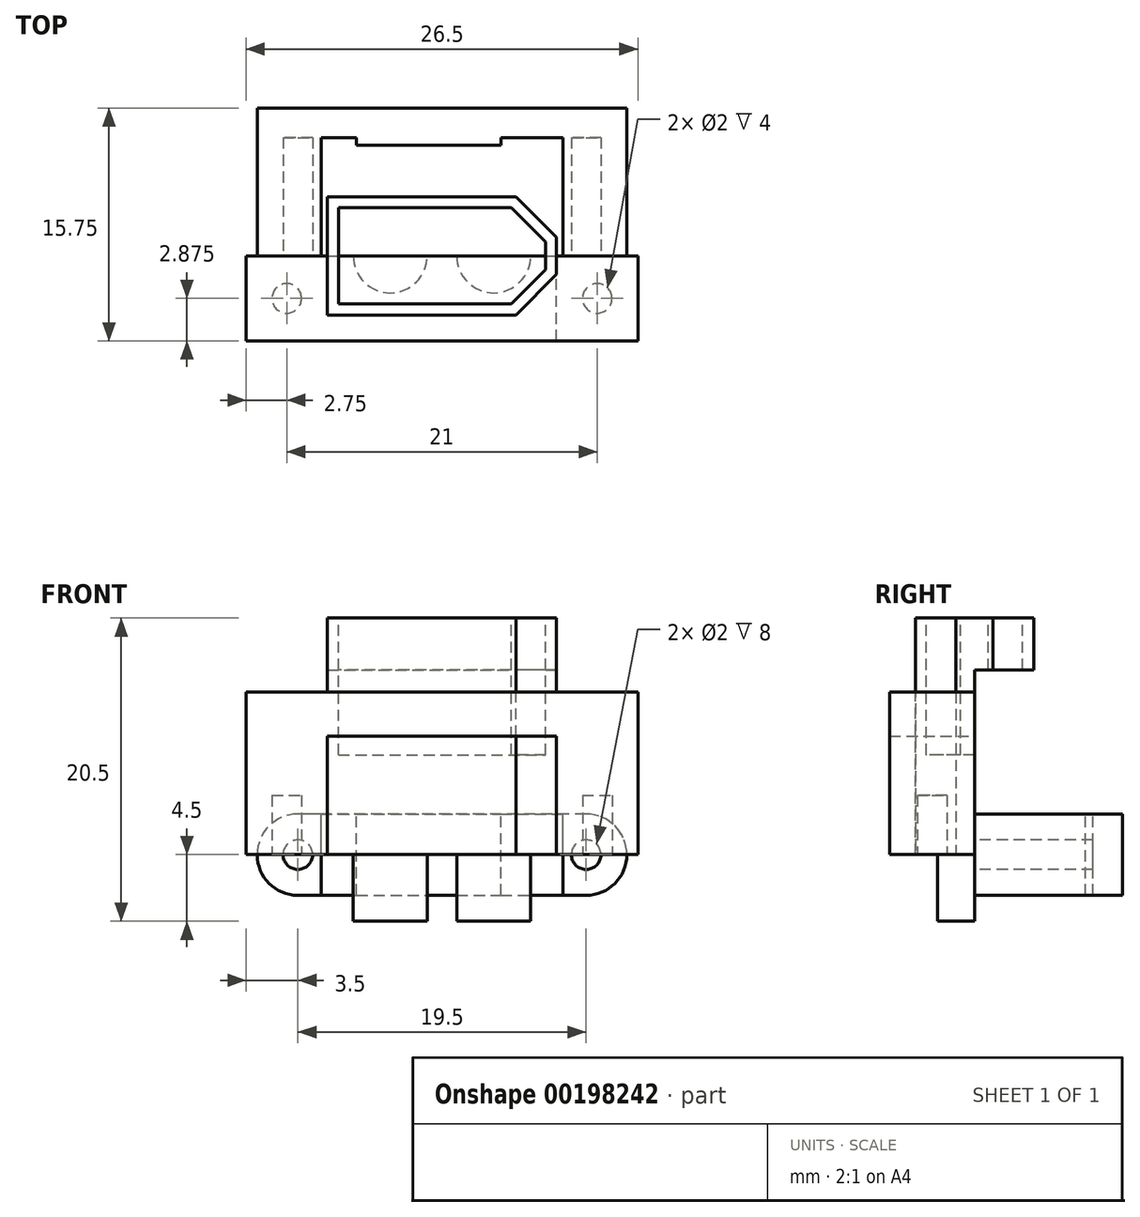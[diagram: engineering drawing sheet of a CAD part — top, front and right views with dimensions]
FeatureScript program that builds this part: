
annotation { "Feature Type Name" : "Feature", "Feature Type Description" : "" }
export const myFeature = defineFeature(function(context is Context, id is Id, definition is map)
    precondition{}
    {
        {
            var Q0;
            Q0=qCreatedBy(makeId("Top.planeOp"),FACE);
            var sketch = newSketch(context, id + "F0", { "sketchPlane" : qUnion([Q0])});
            skLineSegment(sketch, "E0.bottom", {"start": v(-7.75, 4) * mm, "end": v(7.75, 4) * mm});
            skLineSegment(sketch, "E0.top", {"start": v(-7.75, -4) * mm, "end": v(7.75, -4) * mm});
            skLineSegment(sketch, "E0.left", {"start": v(-7.75, 4) * mm, "end": v(-7.75, -4) * mm});
            skLineSegment(sketch, "E0.right", {"start": v(7.75, 4) * mm, "end": v(7.75, -4) * mm});
            skSolve(sketch);
        }
        {
            var Q0;
            Q0=makeQuery(id+"F0.imprint","IMPRINT",FACE,{"disambiguationData":[TD([[makeQuery(id+"F0.imprint","IMPRINT",EDGE,{"derivedFrom":sQuery(id+"F0.wireOp",EDGE,"E0.bottom")}),-1.0]])]});
            extrude(context, id + "F1", {"entities" : qUnion([Q0]), "depth" : 16 * mm});
        }
        {
            var Q0;
            Q0=makeQuery(id+"F1.opExtrude","SWEPT_EDGE",EDGE,{"disambiguationData":[OSD([sQuery(id+"F0.wireOp",EDGE,"E0.top"),sQuery(id+"F0.wireOp",EDGE,"E0.right")])]});
            var Q1;
            Q1=makeQuery(id+"F1.opExtrude","SWEPT_EDGE",EDGE,{"disambiguationData":[OSD([sQuery(id+"F0.wireOp",EDGE,"E0.bottom"),sQuery(id+"F0.wireOp",EDGE,"E0.right")])]});
            chamfer(context, id + "F2", {"entities" : qUnion([Q0, Q1]), "width" : 2.75 * mm, "tangentPropagation" : true});
        }
        {
            var Q0;
            Q0=makeQuery(id+"F1.opExtrude","CAP_FACE",FACE,{"disambiguationData":[OSD([sQuery(id+"F0.wireOp",EDGE,"E0.bottom"),sQuery(id+"F0.wireOp",EDGE,"E0.top"),sQuery(id+"F0.wireOp",EDGE,"E0.left"),sQuery(id+"F0.wireOp",EDGE,"E0.right")])],"isStart":false});
            var sketch = newSketch(context, id + "F3", { "sketchPlane" : qUnion([Q0])});
            skLineSegment(sketch, "E1.bottom", {"start": v(-7, 3.25) * mm, "end": v(4.69, 3.25) * mm});
            skLineSegment(sketch, "E1.top", {"start": v(-7, -3.25) * mm, "end": v(4.69, -3.25) * mm});
            skLineSegment(sketch, "E1.left", {"start": v(-7, 3.25) * mm, "end": v(-7, -3.25) * mm});
            skLineSegment(sketch, "E2", {"start": v(4.69, 3.25) * mm, "end": v(7, 0.94) * mm});
            skLineSegment(sketch, "E3", {"start": v(7, 0.94) * mm, "end": v(7, -0.94) * mm});
            skLineSegment(sketch, "E4", {"start": v(7, -0.94) * mm, "end": v(4.69, -3.25) * mm});
            skSolve(sketch);
        }
        {
            var Q0;
            Q0 = qSketchRegion(id + "F3", true);
            extrude(context, id + "F4", {"entities" : qUnion([Q0]), "operationType" : NewBodyOperationType.REMOVE, "oppositeDirection" : true, "depth" : 9.25 * mm});
        }
        {
            var Q0;
            Q0=makeQuery(id+"F1.opExtrude","CAP_FACE",FACE,{"disambiguationData":[OSD([sQuery(id+"F0.wireOp",EDGE,"E0.bottom"),sQuery(id+"F0.wireOp",EDGE,"E0.top"),sQuery(id+"F0.wireOp",EDGE,"E0.left"),sQuery(id+"F0.wireOp",EDGE,"E0.right")])],"isStart":true});
            var sketch = newSketch(context, id + "F5", { "sketchPlane" : qUnion([Q0])});
            skCircle(sketch, "E5", {"center": v(-3.5, 0) * mm, "radius": 2.5 * mm});
            skCircle(sketch, "E6", {"center": v(3.5, 0) * mm, "radius": 2.5 * mm});
            skSolve(sketch);
        }
        {
            var Q0;
            Q0 = qSketchRegion(id + "F5", true);
            extrude(context, id + "F6", {"entities" : qUnion([Q0]), "operationType" : NewBodyOperationType.ADD, "depth" : 4.5 * mm});
        }
        {
            var Q0;
            Q0=makeQuery(id+"F1.opExtrude","SWEPT_FACE",FACE,{"disambiguationData":[OSD([sQuery(id+"F0.wireOp",EDGE,"E0.bottom")])]});
            var sketch = newSketch(context, id + "F7", { "sketchPlane" : qUnion([Q0])});
            skLineSegment(sketch, "E7.bottom", {"start": v(-3.75, 6.75) * mm, "end": v(6.25, 6.75) * mm});
            skLineSegment(sketch, "E7.top", {"start": v(-3.75, 1) * mm, "end": v(6.25, 1) * mm});
            skLineSegment(sketch, "E7.left", {"start": v(-3.75, 6.75) * mm, "end": v(-3.75, 1) * mm});
            skLineSegment(sketch, "E7.right", {"start": v(6.25, 6.75) * mm, "end": v(6.25, 1) * mm});
            skSolve(sketch);
        }
        {
            var Q0;
            Q0=makeQuery(id+"F7.imprint","IMPRINT",FACE,{"disambiguationData":[TD([[makeQuery(id+"F7.imprint","IMPRINT",EDGE,{"derivedFrom":sQuery(id+"F7.wireOp",EDGE,"E7.bottom")}),-1.0]])]});
            extrude(context, id + "F8", {"entities" : qUnion([Q0]), "operationType" : NewBodyOperationType.REMOVE, "oppositeDirection" : true, "depth" : 0.5 * mm});
        }
        {
            var Q0;
            Q0=qCreatedBy(makeId("Front.planeOp"),FACE);
            var sketch = newSketch(context, id + "F9", { "sketchPlane" : qUnion([Q0])});
            skLineSegment(sketch, "E8.top", {"start": v(-7.75, 8) * mm, "end": v(7.75, 8) * mm});
            skLineSegment(sketch, "E8.left", {"start": v(-7.75, 0) * mm, "end": v(-7.75, 8) * mm});
            skLineSegment(sketch, "E8.right", {"start": v(7.75, 0) * mm, "end": v(7.75, 8) * mm});
            skLineSegment(sketch, "E9.bottom", {"start": v(-13.25, 0) * mm, "end": v(-7.75, 0) * mm});
            skLineSegment(sketch, "E9.top", {"start": v(-13.25, 11) * mm, "end": v(13.25, 11) * mm});
            skLineSegment(sketch, "E9.left", {"start": v(-13.25, 0) * mm, "end": v(-13.25, 11) * mm});
            skLineSegment(sketch, "E9.right", {"start": v(13.25, 0) * mm, "end": v(13.25, 11) * mm});
            skLineSegment(sketch, "E10.trimOffspring", {"start": v(7.75, 0) * mm, "end": v(13.25, 0) * mm});
            skSolve(sketch);
        }
        {
            var Q0;
            Q0 = qSketchRegion(id + "F9", true);
            extrude(context, id + "F10", {"entities" : qUnion([Q0]), "depth" : 5.75 * mm});
        }
        {
            var Q0;
            Q0=makeQuery(id+"F10.opExtrude","SWEPT_FACE",FACE,{"disambiguationData":[OSD([sQuery(id+"F9.wireOp",EDGE,"E9.bottom")])]});
            var sketch = newSketch(context, id + "F11", { "sketchPlane" : qUnion([Q0])});
            skCircle(sketch, "E11", {"center": v(-10.5, 2.88) * mm, "radius": 1 * mm});
            skCircle(sketch, "E12", {"center": v(10.5, 2.88) * mm, "radius": 1 * mm});
            skSolve(sketch);
        }
        {
            var Q0;
            Q0 = qSketchRegion(id + "F11", true);
            extrude(context, id + "F12", {"entities" : qUnion([Q0]), "operationType" : NewBodyOperationType.REMOVE, "oppositeDirection" : true, "depth" : 4 * mm});
        }
        {
            var Q0;
            Q0=qCreatedBy(makeId("Front.planeOp"),FACE);
            var sketch = newSketch(context, id + "F13", { "sketchPlane" : qUnion([Q0])});
            skArc(sketch, "E13", {"start": v(9.75, -2.75) * mm, "mid": v(12.5, 0) * mm, "end": v(9.75, 2.75) * mm});
            skArc(sketch, "E14", {"start": v(-9.75, 2.75) * mm, "mid": v(-12.5, 0) * mm, "end": v(-9.75, -2.75) * mm});
            skLineSegment(sketch, "E15.bottom", {"start": v(9.75, 2.75) * mm, "end": v(-9.75, 2.75) * mm});
            skLineSegment(sketch, "E15.top", {"start": v(9.75, -2.75) * mm, "end": v(-9.75, -2.75) * mm});
            skSolve(sketch);
        }
        {
            var Q0;
            Q0 = qSketchRegion(id + "F13", true);
            extrude(context, id + "F14", {"entities" : qUnion([Q0]), "oppositeDirection" : true, "depth" : 10 * mm});
        }
        {
            var Q0;
            Q0=qCreatedBy(makeId("Top.planeOp"),FACE);
            var sketch = newSketch(context, id + "F15", { "sketchPlane" : qUnion([Q0])});
            skLineSegment(sketch, "E16.bottom", {"start": v(-8.18, 0) * mm, "end": v(8.18, 0) * mm});
            skLineSegment(sketch, "E16.top", {"start": v(-8.18, 8) * mm, "end": v(-5.78, 8) * mm});
            skLineSegment(sketch, "E16.left", {"start": v(-8.18, 0) * mm, "end": v(-8.18, 8) * mm});
            skLineSegment(sketch, "E16.right", {"start": v(8.18, 0) * mm, "end": v(8.18, 8) * mm});
            skLineSegment(sketch, "E17.top", {"start": v(-5.78, 7.5) * mm, "end": v(3.98, 7.5) * mm});
            skLineSegment(sketch, "E17.left", {"start": v(-5.78, 8) * mm, "end": v(-5.78, 7.5) * mm});
            skLineSegment(sketch, "E17.right", {"start": v(3.98, 8) * mm, "end": v(3.98, 7.5) * mm});
            skLineSegment(sketch, "E18.trimOffspring", {"start": v(3.98, 8) * mm, "end": v(8.18, 8) * mm});
            skSolve(sketch);
        }
        {
            var Q0;
            Q0 = qSketchRegion(id + "F15", true);
            extrude(context, id + "F16", {"entities" : qUnion([Q0]), "operationType" : NewBodyOperationType.REMOVE, "endBound" : BoundingType.SYMMETRIC, "oppositeDirection" : true, "depth" : 25 * mm});
        }
        {
            var Q0;
            {var subQ0=sQuery(id+"F13.wireOp",EDGE,"E14");var subQ1=sQuery(id+"F13.wireOp",EDGE,"E15.bottom");var subQ2=sQuery(id+"F13.wireOp",EDGE,"E15.top");Q0=makeQuery(id+"F16.boolean.opBoolean","SPLIT",FACE,{"disambiguationData":[TD([makeQuery(id+"F14.opExtrude","SWEPT_FACE",FACE,{"disambiguationData":[OSD([subQ0])]})])],"derivedFrom":makeQuery(id+"F14.opExtrude","CAP_FACE",FACE,{"disambiguationData":[OSD([sQuery(id+"F13.wireOp",EDGE,"E13"),subQ0,subQ1,subQ2])],"isStart":true})});}
            var sketch = newSketch(context, id + "F17", { "sketchPlane" : qUnion([Q0])});
            skCircle(sketch, "E19", {"center": v(-9.75, 0) * mm, "radius": 1 * mm});
            skCircle(sketch, "E20", {"center": v(9.75, 0) * mm, "radius": 1 * mm});
            skSolve(sketch);
        }
        {
            var Q0;
            Q0 = qSketchRegion(id + "F17", true);
            extrude(context, id + "F18", {"entities" : qUnion([Q0]), "operationType" : NewBodyOperationType.REMOVE, "oppositeDirection" : true, "depth" : 8 * mm});
        }
    });
